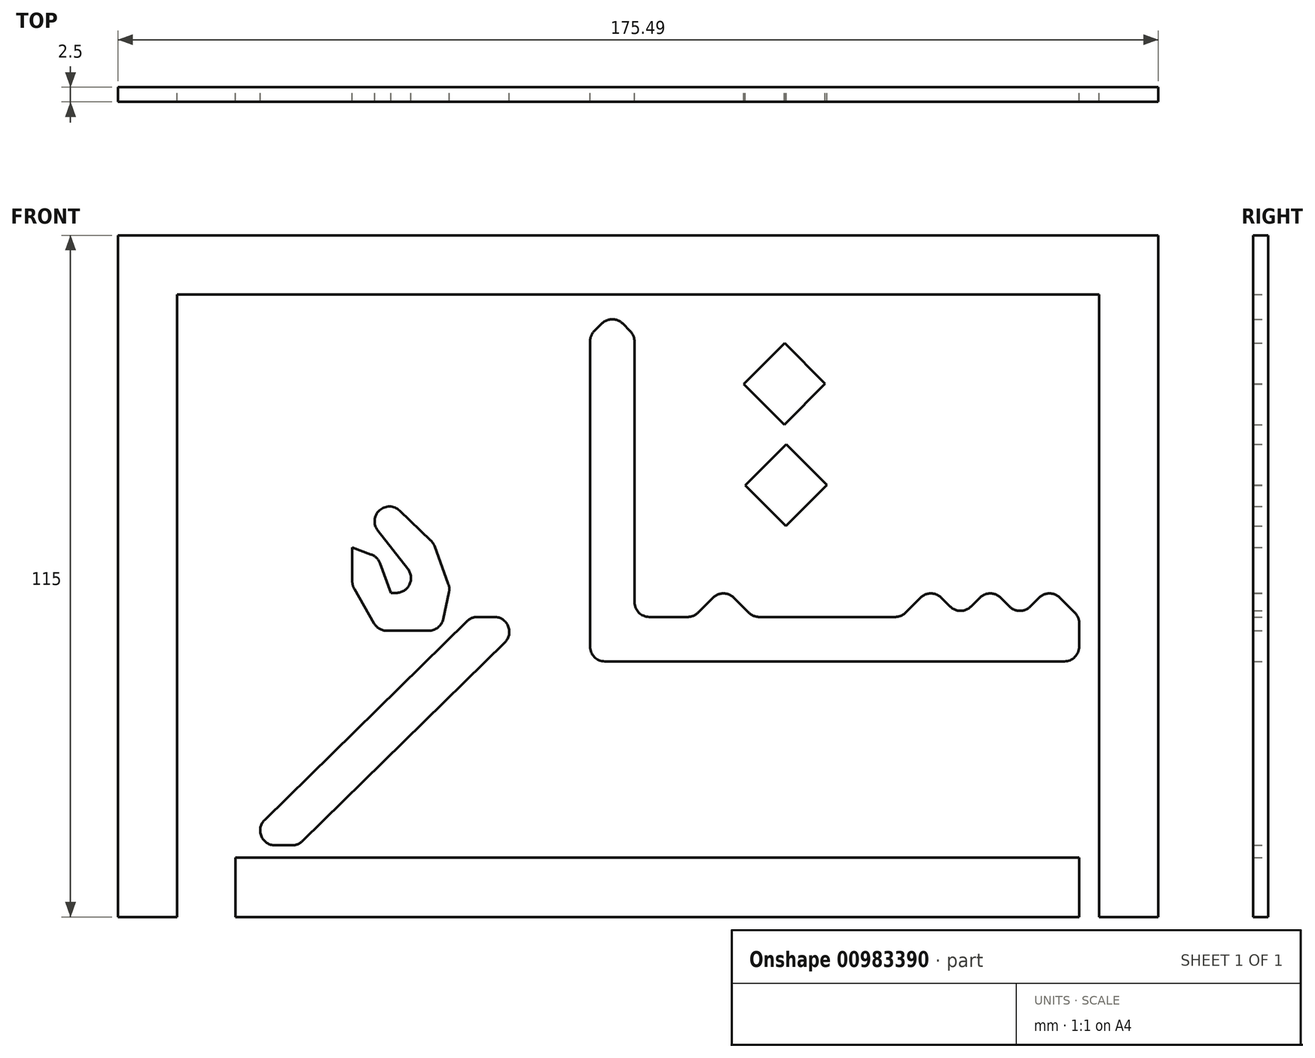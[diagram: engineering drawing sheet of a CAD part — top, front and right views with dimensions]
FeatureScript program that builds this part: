
annotation { "Feature Type Name" : "Feature", "Feature Type Description" : "" }
export const myFeature = defineFeature(function(context is Context, id is Id, definition is map)
    precondition{}
    {
        {
            var Q0;
            Q0=qCreatedBy(makeId("Front.planeOp"),FACE);
            var sketch = newSketch(context, id + "F0", { "sketchPlane" : qUnion([Q0])});
            skLineSegment(sketch, "E0", {"start": v(0, -2.07) * mm, "end": v(0, -10) * mm});
            skLineSegment(sketch, "E1", {"start": v(-5, -15) * mm, "end": v(-160, -15) * mm});
            skLineSegment(sketch, "E2", {"start": v(-165, -10) * mm, "end": v(-165, 92.93) * mm});
            skLineSegment(sketch, "E3", {"start": v(-163.54, 96.46) * mm, "end": v(-161.04, 98.96) * mm});
            skLineSegment(sketch, "E4", {"start": v(-153.96, 98.96) * mm, "end": v(-151.46, 96.46) * mm});
            skLineSegment(sketch, "E5", {"start": v(-150, 92.93) * mm, "end": v(-150, 5) * mm});
            skLineSegment(sketch, "E6", {"start": v(-145, 0) * mm, "end": v(-132.07, 0) * mm});
            skLineSegment(sketch, "E7", {"start": v(-128.54, 1.46) * mm, "end": v(-123.54, 6.46) * mm});
            skLineSegment(sketch, "E8", {"start": v(-116.46, 6.46) * mm, "end": v(-111.46, 1.46) * mm});
            skLineSegment(sketch, "E9", {"start": v(-107.93, 0) * mm, "end": v(-62.07, 0) * mm});
            skLineSegment(sketch, "E10", {"start": v(-58.54, 1.46) * mm, "end": v(-53.54, 6.46) * mm});
            skLineSegment(sketch, "E11", {"start": v(-46.46, 6.46) * mm, "end": v(-43.54, 3.54) * mm});
            skLineSegment(sketch, "E12", {"start": v(-36.46, 3.54) * mm, "end": v(-33.54, 6.46) * mm});
            skLineSegment(sketch, "E13", {"start": v(-26.46, 6.46) * mm, "end": v(-23.54, 3.54) * mm});
            skLineSegment(sketch, "E14", {"start": v(-16.46, 3.54) * mm, "end": v(-13.54, 6.46) * mm});
            skLineSegment(sketch, "E15", {"start": v(-6.46, 6.46) * mm, "end": v(-1.46, 1.46) * mm});
            skPoint(sketch, "E16.visualSharp", {"position": v(-165, 95) * mm});
            skArc(sketch, "E16.filletArc", {"start": v(-163.54, 96.46) * mm, "mid": v(-164.62, 94.84) * mm, "end": v(-165, 92.93) * mm});
            skPoint(sketch, "E17.visualSharp", {"position": v(-157.5, 102.5) * mm});
            skArc(sketch, "E17.filletArc", {"start": v(-153.96, 98.96) * mm, "mid": v(-157.5, 100.43) * mm, "end": v(-161.04, 98.96) * mm});
            skPoint(sketch, "E18.visualSharp", {"position": v(-150, 95) * mm});
            skArc(sketch, "E18.filletArc", {"start": v(-150, 92.93) * mm, "mid": v(-150.38, 94.84) * mm, "end": v(-151.46, 96.46) * mm});
            skPoint(sketch, "E19.visualSharp", {"position": v(-150, 0) * mm});
            skArc(sketch, "E19.filletArc", {"start": v(-150, 5) * mm, "mid": v(-148.54, 1.46) * mm, "end": v(-145, 0) * mm});
            skPoint(sketch, "E20.visualSharp", {"position": v(-130, 0) * mm});
            skArc(sketch, "E20.filletArc", {"start": v(-132.07, 0) * mm, "mid": v(-130.16, 0.38) * mm, "end": v(-128.54, 1.46) * mm});
            skPoint(sketch, "E21.visualSharp", {"position": v(-120, 10) * mm});
            skArc(sketch, "E21.filletArc", {"start": v(-116.46, 6.46) * mm, "mid": v(-120, 7.93) * mm, "end": v(-123.54, 6.46) * mm});
            skPoint(sketch, "E22.visualSharp", {"position": v(-110, 0) * mm});
            skArc(sketch, "E22.filletArc", {"start": v(-111.46, 1.46) * mm, "mid": v(-109.84, 0.38) * mm, "end": v(-107.93, 0) * mm});
            skPoint(sketch, "E23.visualSharp", {"position": v(-60, 0) * mm});
            skArc(sketch, "E23.filletArc", {"start": v(-62.07, 0) * mm, "mid": v(-60.16, 0.38) * mm, "end": v(-58.54, 1.46) * mm});
            skPoint(sketch, "E24.visualSharp", {"position": v(-50, 10) * mm});
            skArc(sketch, "E24.filletArc", {"start": v(-46.46, 6.46) * mm, "mid": v(-50, 7.93) * mm, "end": v(-53.54, 6.46) * mm});
            skPoint(sketch, "E25.visualSharp", {"position": v(-40, 0) * mm});
            skArc(sketch, "E25.filletArc", {"start": v(-43.54, 3.54) * mm, "mid": v(-40, 2.07) * mm, "end": v(-36.46, 3.54) * mm});
            skPoint(sketch, "E26.visualSharp", {"position": v(-30, 10) * mm});
            skArc(sketch, "E26.filletArc", {"start": v(-26.46, 6.46) * mm, "mid": v(-30, 7.93) * mm, "end": v(-33.54, 6.46) * mm});
            skPoint(sketch, "E27.visualSharp", {"position": v(-20, 0) * mm});
            skArc(sketch, "E27.filletArc", {"start": v(-23.54, 3.54) * mm, "mid": v(-20, 2.07) * mm, "end": v(-16.46, 3.54) * mm});
            skPoint(sketch, "E28.visualSharp", {"position": v(-10, 10) * mm});
            skArc(sketch, "E28.filletArc", {"start": v(-6.46, 6.46) * mm, "mid": v(-10, 7.93) * mm, "end": v(-13.54, 6.46) * mm});
            skPoint(sketch, "E29.visualSharp", {"position": v(0, 0) * mm});
            skArc(sketch, "E29.filletArc", {"start": v(0, -2.07) * mm, "mid": v(-0.38, -0.16) * mm, "end": v(-1.46, 1.46) * mm});
            skPoint(sketch, "E30.visualSharp", {"position": v(0, -15) * mm});
            skArc(sketch, "E30.filletArc", {"start": v(-5, -15) * mm, "mid": v(-1.46, -13.54) * mm, "end": v(0, -10) * mm});
            skPoint(sketch, "E31.visualSharp", {"position": v(-165, -15) * mm});
            skArc(sketch, "E31.filletArc", {"start": v(-165, -10) * mm, "mid": v(-163.54, -13.54) * mm, "end": v(-160, -15) * mm});
            skLineSegment(sketch, "E32", {"start": v(-197.23, 0) * mm, "end": v(-202.96, 0) * mm});
            skLineSegment(sketch, "E33", {"start": v(-206.46, -1.43) * mm, "end": v(-274.76, -68.5) * mm});
            skLineSegment(sketch, "E34", {"start": v(-271.26, -77.07) * mm, "end": v(-265.53, -77.07) * mm});
            skLineSegment(sketch, "E35", {"start": v(-262.03, -75.64) * mm, "end": v(-193.73, -8.57) * mm});
            skPoint(sketch, "E36.visualSharp", {"position": v(-205, 0) * mm});
            skArc(sketch, "E36.filletArc", {"start": v(-202.96, 0) * mm, "mid": v(-204.85, -0.37) * mm, "end": v(-206.46, -1.43) * mm});
            skPoint(sketch, "E37.visualSharp", {"position": v(-185, 0) * mm});
            skArc(sketch, "E37.filletArc", {"start": v(-193.73, -8.57) * mm, "mid": v(-192.6, -3.1) * mm, "end": v(-197.23, 0) * mm});
            skPoint(sketch, "E38.visualSharp", {"position": v(-263.49, -77.07) * mm});
            skArc(sketch, "E38.filletArc", {"start": v(-265.53, -77.07) * mm, "mid": v(-263.64, -76.7) * mm, "end": v(-262.03, -75.64) * mm});
            skPoint(sketch, "E39.visualSharp", {"position": v(-283.49, -77.07) * mm});
            skArc(sketch, "E39.filletArc", {"start": v(-274.76, -68.5) * mm, "mid": v(-275.89, -73.96) * mm, "end": v(-271.26, -77.07) * mm});
            skLineSegment(sketch, "E40", {"start": v(-229.2, 35.87) * mm, "end": v(-218.7, 25.78) * mm});
            skLineSegment(sketch, "E41", {"start": v(-217.47, 23.9) * mm, "end": v(-212.78, 11.17) * mm});
            skLineSegment(sketch, "E42", {"start": v(-212.59, 8.38) * mm, "end": v(-214.55, -0.72) * mm});
            skLineSegment(sketch, "E43", {"start": v(-219.44, -4.66) * mm, "end": v(-233.5, -4.66) * mm});
            skLineSegment(sketch, "E44", {"start": v(-237.83, -2.15) * mm, "end": v(-244.52, 9.5) * mm});
            skLineSegment(sketch, "E45", {"start": v(-245.19, 11.99) * mm, "end": v(-245.19, 23.42) * mm});
            skLineSegment(sketch, "E46", {"start": v(-245.19, 23.42) * mm, "end": v(-238.84, 21.1) * mm});
            skLineSegment(sketch, "E47", {"start": v(-235.87, 18.14) * mm, "end": v(-232.14, 8.1) * mm});
            skLineSegment(sketch, "E48", {"start": v(-232.14, 8.1) * mm, "end": v(-230.39, 8.1) * mm});
            skLineSegment(sketch, "E49", {"start": v(-226.45, 16.18) * mm, "end": v(-236.61, 29.18) * mm});
            skPoint(sketch, "E50.visualSharp", {"position": v(-279.92, 84.58) * mm});
            skArc(sketch, "E50.filletArc", {"start": v(-229.2, 35.87) * mm, "mid": v(-236.02, 35.97) * mm, "end": v(-236.61, 29.18) * mm});
            skPoint(sketch, "E51.visualSharp", {"position": v(-217.87, 24.98) * mm});
            skArc(sketch, "E51.filletArc", {"start": v(-217.47, 23.9) * mm, "mid": v(-217.98, 24.9) * mm, "end": v(-218.7, 25.78) * mm});
            skPoint(sketch, "E52.visualSharp", {"position": v(-212.28, 9.8) * mm});
            skArc(sketch, "E52.filletArc", {"start": v(-212.59, 8.38) * mm, "mid": v(-212.49, 9.79) * mm, "end": v(-212.78, 11.17) * mm});
            skPoint(sketch, "E53.visualSharp", {"position": v(-215.4, -4.66) * mm});
            skArc(sketch, "E53.filletArc", {"start": v(-219.44, -4.66) * mm, "mid": v(-216.3, -3.55) * mm, "end": v(-214.55, -0.72) * mm});
            skPoint(sketch, "E54.visualSharp", {"position": v(-220.13, 8.1) * mm});
            skArc(sketch, "E54.filletArc", {"start": v(-230.39, 8.1) * mm, "mid": v(-225.9, 10.9) * mm, "end": v(-226.45, 16.18) * mm});
            skPoint(sketch, "E55.visualSharp", {"position": v(-236.68, 20.3) * mm});
            skArc(sketch, "E55.filletArc", {"start": v(-235.87, 18.14) * mm, "mid": v(-237.03, 19.94) * mm, "end": v(-238.84, 21.1) * mm});
            skPoint(sketch, "E56.visualSharp", {"position": v(-245.19, 10.65) * mm});
            skArc(sketch, "E56.filletArc", {"start": v(-245.19, 11.99) * mm, "mid": v(-245.02, 10.7) * mm, "end": v(-244.52, 9.5) * mm});
            skPoint(sketch, "E57.visualSharp", {"position": v(-236.4, -4.66) * mm});
            skArc(sketch, "E57.filletArc", {"start": v(-237.83, -2.15) * mm, "mid": v(-236, -4) * mm, "end": v(-233.5, -4.66) * mm});
            skLineSegment(sketch, "E58.bottom", {"start": v(-99.33, 92.37) * mm, "end": v(-85.67, 78.7) * mm});
            skLineSegment(sketch, "E58.top", {"start": v(-113.16, 78.54) * mm, "end": v(-99.5, 64.88) * mm});
            skLineSegment(sketch, "E58.left", {"start": v(-99.33, 92.37) * mm, "end": v(-113.16, 78.54) * mm});
            skLineSegment(sketch, "E58.right", {"start": v(-85.67, 78.7) * mm, "end": v(-99.5, 64.88) * mm});
            skLineSegment(sketch, "E59.bottom", {"start": v(-98.76, 58.22) * mm, "end": v(-85.1, 44.56) * mm});
            skLineSegment(sketch, "E59.top", {"start": v(-112.6, 44.39) * mm, "end": v(-98.93, 30.73) * mm});
            skLineSegment(sketch, "E59.left", {"start": v(-98.76, 58.22) * mm, "end": v(-112.6, 44.39) * mm});
            skLineSegment(sketch, "E59.right", {"start": v(-85.1, 44.56) * mm, "end": v(-98.93, 30.73) * mm});
            skLineSegment(sketch, "E60.bottom", {"start": v(-324.24, -101.22) * mm, "end": v(-304.24, -101.22) * mm});
            skLineSegment(sketch, "E60.top", {"start": v(-324.24, 128.78) * mm, "end": v(-304.24, 128.78) * mm});
            skLineSegment(sketch, "E60.left", {"start": v(-324.24, -101.22) * mm, "end": v(-324.24, 128.78) * mm});
            skLineSegment(sketch, "E60.right", {"start": v(-304.24, -101.22) * mm, "end": v(-304.24, 128.78) * mm});
            skLineSegment(sketch, "E61.bottom", {"start": v(-304.24, 128.78) * mm, "end": v(6.74, 128.78) * mm});
            skLineSegment(sketch, "E61.top", {"start": v(-304.24, 108.78) * mm, "end": v(6.74, 108.78) * mm});
            skLineSegment(sketch, "E61.left", {"start": v(-304.24, 128.78) * mm, "end": v(-304.24, 108.78) * mm});
            skLineSegment(sketch, "E61.right", {"start": v(6.74, 128.78) * mm, "end": v(6.74, 108.78) * mm});
            skLineSegment(sketch, "E62.bottom", {"start": v(6.74, 128.78) * mm, "end": v(26.74, 128.78) * mm});
            skLineSegment(sketch, "E62.top", {"start": v(6.74, -101.22) * mm, "end": v(26.74, -101.22) * mm});
            skLineSegment(sketch, "E62.left", {"start": v(6.74, 128.78) * mm, "end": v(6.74, -101.22) * mm});
            skLineSegment(sketch, "E62.right", {"start": v(26.74, 128.78) * mm, "end": v(26.74, -101.22) * mm});
            skLineSegment(sketch, "E63.bottom", {"start": v(-284.54, -81.22) * mm, "end": v(0, -81.22) * mm});
            skLineSegment(sketch, "E63.top", {"start": v(-284.54, -101.22) * mm, "end": v(0, -101.22) * mm});
            skLineSegment(sketch, "E63.left", {"start": v(-284.54, -81.22) * mm, "end": v(-284.54, -101.22) * mm});
            skLineSegment(sketch, "E63.right", {"start": v(0, -81.22) * mm, "end": v(0, -101.22) * mm});
            skSolve(sketch);
        }
        {
            var Q0;
            Q0 = qSketchRegion(id + "F0", true);
            extrude(context, id + "F1", {"entities" : qUnion([Q0]), "depth" : 5 * mm, "offsetDistance" : 25 * mm});
        }
        {
            var Q0;
            Q0=makeQuery(id+"F1.opExtrude","SWEPT_BODY",BODY,{"disambiguationData":[OSD([sQuery(id+"F0.wireOp",EDGE,"E60.bottom"),sQuery(id+"F0.wireOp",EDGE,"E60.top"),sQuery(id+"F0.wireOp",EDGE,"E60.left"),sQuery(id+"F0.wireOp",EDGE,"E60.right"),sQuery(id+"F0.wireOp",EDGE,"E61.bottom"),sQuery(id+"F0.wireOp",EDGE,"E61.top"),sQuery(id+"F0.wireOp",EDGE,"E62.bottom"),sQuery(id+"F0.wireOp",EDGE,"E62.top"),sQuery(id+"F0.wireOp",EDGE,"E62.left"),sQuery(id+"F0.wireOp",EDGE,"E62.right")])]});
            var Q1;
            Q1=makeQuery(id+"F1.opExtrude","SWEPT_BODY",BODY,{"disambiguationData":[OSD([sQuery(id+"F0.wireOp",EDGE,"E0"),sQuery(id+"F0.wireOp",EDGE,"E1"),sQuery(id+"F0.wireOp",EDGE,"E2"),sQuery(id+"F0.wireOp",EDGE,"E3"),sQuery(id+"F0.wireOp",EDGE,"E4"),sQuery(id+"F0.wireOp",EDGE,"E5"),sQuery(id+"F0.wireOp",EDGE,"E6"),sQuery(id+"F0.wireOp",EDGE,"E7"),sQuery(id+"F0.wireOp",EDGE,"E8"),sQuery(id+"F0.wireOp",EDGE,"E9"),sQuery(id+"F0.wireOp",EDGE,"E10"),sQuery(id+"F0.wireOp",EDGE,"E11"),sQuery(id+"F0.wireOp",EDGE,"E12"),sQuery(id+"F0.wireOp",EDGE,"E13"),sQuery(id+"F0.wireOp",EDGE,"E14"),sQuery(id+"F0.wireOp",EDGE,"E15"),sQuery(id+"F0.wireOp",EDGE,"E16.filletArc"),sQuery(id+"F0.wireOp",EDGE,"E17.filletArc"),sQuery(id+"F0.wireOp",EDGE,"E18.filletArc"),sQuery(id+"F0.wireOp",EDGE,"E19.filletArc"),sQuery(id+"F0.wireOp",EDGE,"E20.filletArc"),sQuery(id+"F0.wireOp",EDGE,"E21.filletArc"),sQuery(id+"F0.wireOp",EDGE,"E22.filletArc"),sQuery(id+"F0.wireOp",EDGE,"E23.filletArc"),sQuery(id+"F0.wireOp",EDGE,"E24.filletArc"),sQuery(id+"F0.wireOp",EDGE,"E25.filletArc"),sQuery(id+"F0.wireOp",EDGE,"E26.filletArc"),sQuery(id+"F0.wireOp",EDGE,"E27.filletArc"),sQuery(id+"F0.wireOp",EDGE,"E28.filletArc"),sQuery(id+"F0.wireOp",EDGE,"E29.filletArc"),sQuery(id+"F0.wireOp",EDGE,"E30.filletArc"),sQuery(id+"F0.wireOp",EDGE,"E31.filletArc")])]});
            var Q2;
            Q2=makeQuery(id+"F1.opExtrude","SWEPT_BODY",BODY,{"disambiguationData":[OSD([sQuery(id+"F0.wireOp",EDGE,"E58.bottom"),sQuery(id+"F0.wireOp",EDGE,"E58.top"),sQuery(id+"F0.wireOp",EDGE,"E58.left"),sQuery(id+"F0.wireOp",EDGE,"E58.right")])]});
            var Q3;
            Q3=makeQuery(id+"F1.opExtrude","SWEPT_BODY",BODY,{"disambiguationData":[OSD([sQuery(id+"F0.wireOp",EDGE,"E59.bottom"),sQuery(id+"F0.wireOp",EDGE,"E59.top"),sQuery(id+"F0.wireOp",EDGE,"E59.left"),sQuery(id+"F0.wireOp",EDGE,"E59.right")])]});
            var Q4;
            Q4=makeQuery(id+"F1.opExtrude","SWEPT_BODY",BODY,{"disambiguationData":[OSD([sQuery(id+"F0.wireOp",EDGE,"E40"),sQuery(id+"F0.wireOp",EDGE,"E41"),sQuery(id+"F0.wireOp",EDGE,"E42"),sQuery(id+"F0.wireOp",EDGE,"E43"),sQuery(id+"F0.wireOp",EDGE,"E44"),sQuery(id+"F0.wireOp",EDGE,"E45"),sQuery(id+"F0.wireOp",EDGE,"E46"),sQuery(id+"F0.wireOp",EDGE,"E47"),sQuery(id+"F0.wireOp",EDGE,"E48"),sQuery(id+"F0.wireOp",EDGE,"E49"),sQuery(id+"F0.wireOp",EDGE,"E50.filletArc"),sQuery(id+"F0.wireOp",EDGE,"E51.filletArc"),sQuery(id+"F0.wireOp",EDGE,"E52.filletArc"),sQuery(id+"F0.wireOp",EDGE,"E53.filletArc"),sQuery(id+"F0.wireOp",EDGE,"E54.filletArc"),sQuery(id+"F0.wireOp",EDGE,"E55.filletArc"),sQuery(id+"F0.wireOp",EDGE,"E56.filletArc"),sQuery(id+"F0.wireOp",EDGE,"E57.filletArc")])]});
            var Q5;
            Q5=makeQuery(id+"F1.opExtrude","SWEPT_BODY",BODY,{"disambiguationData":[OSD([sQuery(id+"F0.wireOp",EDGE,"E32"),sQuery(id+"F0.wireOp",EDGE,"E33"),sQuery(id+"F0.wireOp",EDGE,"E34"),sQuery(id+"F0.wireOp",EDGE,"E35"),sQuery(id+"F0.wireOp",EDGE,"E36.filletArc"),sQuery(id+"F0.wireOp",EDGE,"E37.filletArc"),sQuery(id+"F0.wireOp",EDGE,"E38.filletArc"),sQuery(id+"F0.wireOp",EDGE,"E39.filletArc")])]});
            var Q6;
            Q6=makeQuery(id+"F1.opExtrude","SWEPT_BODY",BODY,{"disambiguationData":[OSD([sQuery(id+"F0.wireOp",EDGE,"E63.bottom"),sQuery(id+"F0.wireOp",EDGE,"E63.top"),sQuery(id+"F0.wireOp",EDGE,"E63.left"),sQuery(id+"F0.wireOp",EDGE,"E63.right")])]});
            var Q7;
            Q7=qCreatedBy(makeId("Origin.pointOp"),VERTEX);
            transform(context, id + "F2", {"entities" : qUnion([Q0, Q1, Q2, Q3, Q4, Q5, Q6]), "transformType" : TransformType.SCALE_UNIFORMLY, "scale" : 0.5, "scalePoint" : qUnion([Q7]), "makeCopy" : false});
        }
    });
